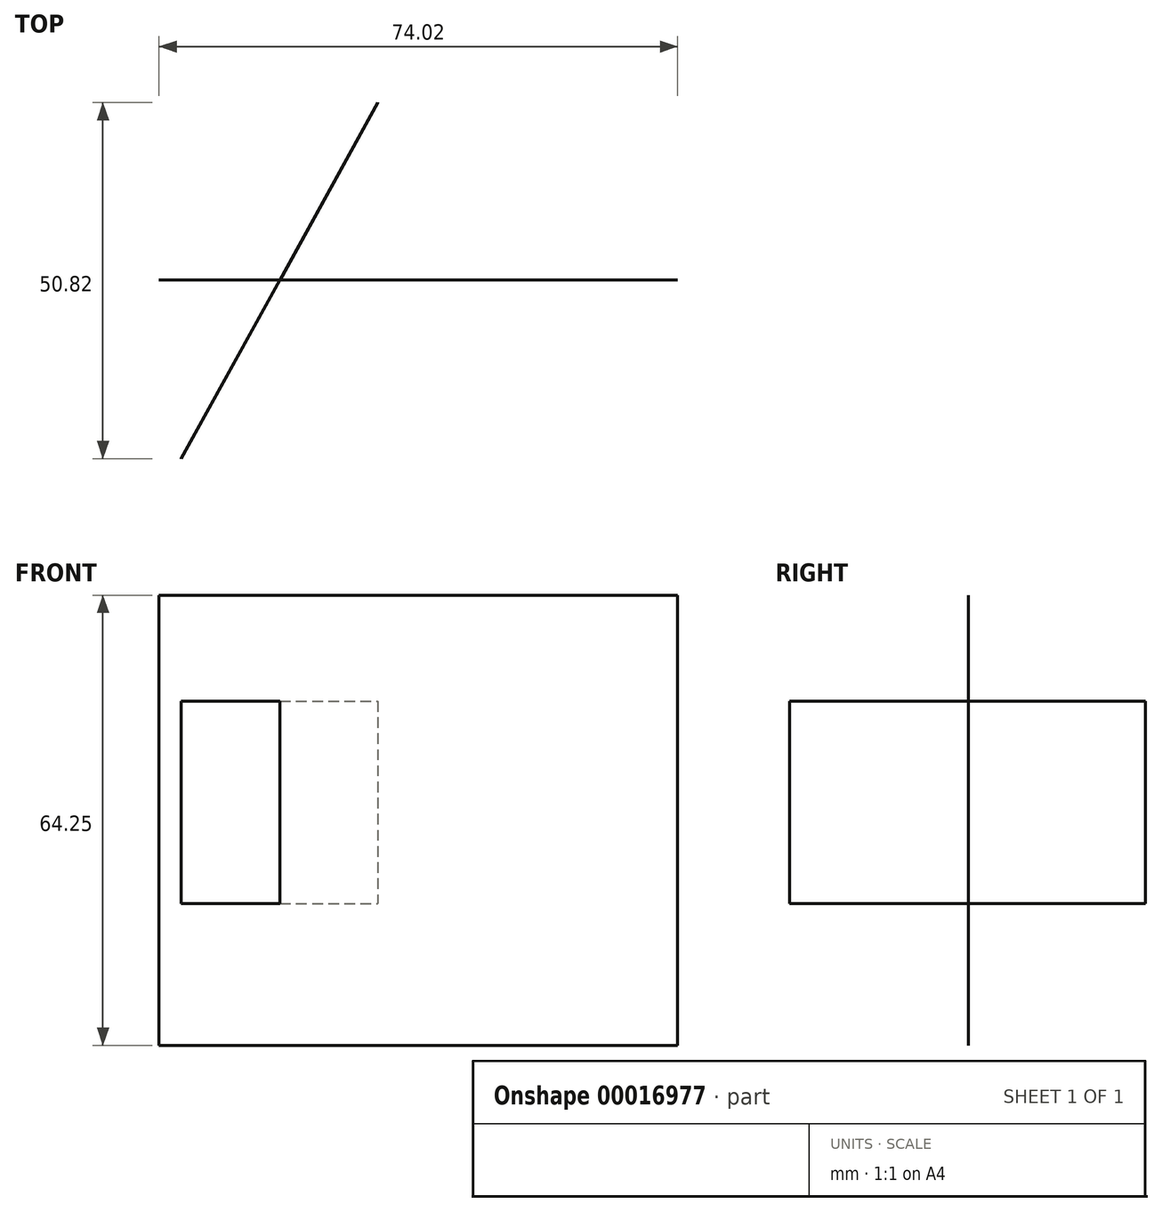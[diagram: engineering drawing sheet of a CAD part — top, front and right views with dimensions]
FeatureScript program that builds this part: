
annotation { "Feature Type Name" : "Feature", "Feature Type Description" : "" }
export const myFeature = defineFeature(function(context is Context, id is Id, definition is map)
    precondition{}
    {
        {
            var Q0;
            Q0=qCreatedBy(makeId("Front.planeOp"),FACE);
            var sketch = newSketch(context, id + "F0", { "sketchPlane" : qUnion([Q0])});
            skLineSegment(sketch, "E0.bottom", {"start": v(-245.71, 75.06) * mm, "end": v(-171.69, 75.06) * mm});
            skLineSegment(sketch, "E0.top", {"start": v(-245.71, 10.8) * mm, "end": v(-171.69, 10.8) * mm});
            skLineSegment(sketch, "E0.left", {"start": v(-245.71, 75.06) * mm, "end": v(-245.71, 10.8) * mm});
            skLineSegment(sketch, "E0.right", {"start": v(-171.69, 75.06) * mm, "end": v(-171.69, 10.8) * mm});
            skSolve(sketch);
        }
        {
            var Q0;
            Q0=makeQuery(id+"F0.imprint","IMPRINT",FACE,{"disambiguationData":[TD([[makeQuery(id+"F0.imprint","IMPRINT",EDGE,{"derivedFrom":sQuery(id+"F0.wireOp",EDGE,"E0.bottom")}),-1.0]])]});
            var sketch = newSketch(context, id + "F1", { "sketchPlane" : qUnion([Q0])});
            skPoint(sketch, "E1", {"position": v(-228.45, 59.88) * mm});
            skPoint(sketch, "E2", {"position": v(-228.45, 31.27) * mm});
            skPoint(sketch, "E3", {"position": v(-208.87, 45.8) * mm});
            skSolve(sketch);
        }
        {
            var Q0;
            Q0=makeQuery(id+"F0.imprint","IMPRINT",FACE,{"disambiguationData":[TD([[makeQuery(id+"F0.imprint","IMPRINT",EDGE,{"derivedFrom":sQuery(id+"F0.wireOp",EDGE,"E0.bottom")}),-1.0]])]});
            cPlane(context, id + "F2", {"entities" : qUnion([Q0]), "cplaneType" : CPlaneType.OFFSET, "offset" : 25.4 * mm, "width" : 152.4 * mm, "height" : 152.4 * mm});
        }
        {
            var Q0;
            Q0=qCreatedBy(id+"F2.planeOp",FACE);
            var sketch = newSketch(context, id + "F3", { "sketchPlane" : qUnion([Q0])});
            skPoint(sketch, "E4", {"position": v(-242.48, 46.61) * mm});
            skSolve(sketch);
        }
        {
            var Q0;
            Q0=sQuery(id+"F3.wireOp",VERTEX,"E4");
            var Q1;
            Q1=sQuery(id+"F1.wireOp",VERTEX,"E1");
            var Q2;
            Q2=sQuery(id+"F1.wireOp",VERTEX,"E2");
            cPlane(context, id + "F4", {"entities" : qUnion([Q0, Q1, Q2]), "cplaneType" : CPlaneType.THREE_POINT, "offset" : 152.4 * mm, "width" : 152.4 * mm, "height" : 152.4 * mm});
        }
        {
            var Q0;
            Q0=qCreatedBy(id+"F4.planeOp",FACE);
            var sketch = newSketch(context, id + "F5", { "sketchPlane" : qUnion([Q0])});
            skLineSegment(sketch, "E5.bottom", {"start": v(-139.62, 59.94) * mm, "end": v(-81.59, 59.94) * mm});
            skLineSegment(sketch, "E5.top", {"start": v(-139.62, 31.04) * mm, "end": v(-81.59, 31.04) * mm});
            skLineSegment(sketch, "E5.left", {"start": v(-139.62, 59.94) * mm, "end": v(-139.62, 31.04) * mm});
            skLineSegment(sketch, "E5.right", {"start": v(-81.59, 59.94) * mm, "end": v(-81.59, 31.04) * mm});
            skSolve(sketch);
        }
        {
            var Q0;
            Q0=makeQuery(id+"F0.imprint","IMPRINT",FACE,{"disambiguationData":[TD([[makeQuery(id+"F0.imprint","IMPRINT",EDGE,{"derivedFrom":sQuery(id+"F0.wireOp",EDGE,"E0.bottom")}),-1.0]])]});
            extrude(context, id + "F6", {"entities" : qUnion([Q0]), "depth" : 0.03 * mm});
        }
        {
            var Q0;
            Q0 = qSketchRegion(id + "F5", true);
            extrude(context, id + "F7", {"entities" : qUnion([Q0]), "operationType" : NewBodyOperationType.ADD, "depth" : 0.03 * mm});
        }
    });
